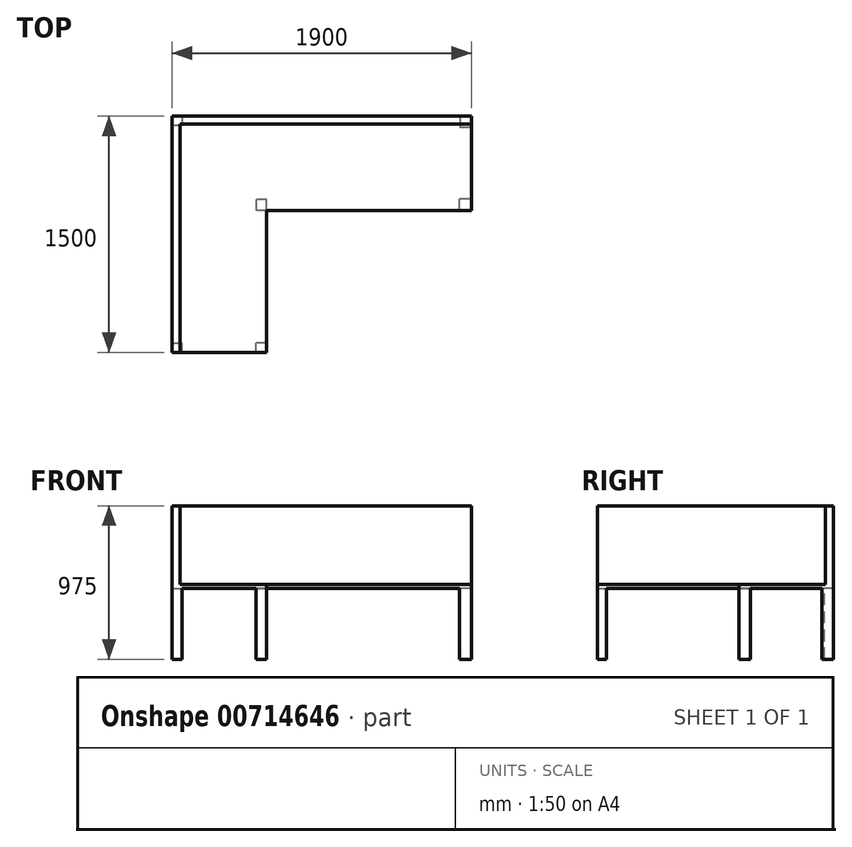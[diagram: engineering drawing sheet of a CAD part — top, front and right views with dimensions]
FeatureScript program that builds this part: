
annotation { "Feature Type Name" : "Feature", "Feature Type Description" : "" }
export const myFeature = defineFeature(function(context is Context, id is Id, definition is map)
    precondition{}
    {
        {
            var Q0;
            Q0=qCreatedBy(makeId("Top.planeOp"),FACE);
            var sketch = newSketch(context, id + "F0", { "sketchPlane" : qUnion([Q0])});
            skLineSegment(sketch, "E0.bottom", {"start": v(0, 0) * mm, "end": v(1900, 0) * mm});
            skLineSegment(sketch, "E0.top", {"start": v(600, -600) * mm, "end": v(1900, -600) * mm});
            skLineSegment(sketch, "E0.left", {"start": v(0, 0) * mm, "end": v(0, -600) * mm});
            skLineSegment(sketch, "E0.right", {"start": v(1900, 0) * mm, "end": v(1900, -600) * mm});
            skLineSegment(sketch, "E1.top", {"start": v(0, -1500) * mm, "end": v(600, -1500) * mm});
            skLineSegment(sketch, "E1.left", {"start": v(0, -600) * mm, "end": v(0, -1500) * mm});
            skLineSegment(sketch, "E1.right", {"start": v(600, -600) * mm, "end": v(600, -1500) * mm});
            skSolve(sketch);
        }
        {
            var Q0;
            Q0=makeQuery(id+"F0.imprint","IMPRINT",FACE,{"disambiguationData":[TD([[makeQuery(id+"F0.imprint","IMPRINT",EDGE,{"derivedFrom":sQuery(id+"F0.wireOp",EDGE,"E0.bottom")}),-1.0]])]});
            extrude(context, id + "F1", {"entities" : qUnion([Q0]), "depth" : 25 * mm, "offsetDistance" : 25 * mm});
        }
        {
            var Q0;
            Q0=makeQuery(id+"F1.opExtrude","CAP_FACE",FACE,{"disambiguationData":[OSD([sQuery(id+"F0.wireOp",EDGE,"E0.bottom"),sQuery(id+"F0.wireOp",EDGE,"E0.top"),sQuery(id+"F0.wireOp",EDGE,"E0.left"),sQuery(id+"F0.wireOp",EDGE,"E0.right"),sQuery(id+"F0.wireOp",EDGE,"vzaPsGMV-BrJu-azBP-gitS-3Vx8ohO2lJfg.top"),sQuery(id+"F0.wireOp",EDGE,"vzaPsGMV-BrJu-azBP-gitS-3Vx8ohO2lJfg.left"),sQuery(id+"F0.wireOp",EDGE,"vzaPsGMV-BrJu-azBP-gitS-3Vx8ohO2lJfg.right")])],"isStart":false});
            var sketch = newSketch(context, id + "F2", { "sketchPlane" : qUnion([Q0])});
            skLineSegment(sketch, "E2.bottom", {"start": v(1900, 0) * mm, "end": v(0, 0) * mm});
            skLineSegment(sketch, "E2.top", {"start": v(1900, -50) * mm, "end": v(50, -50) * mm});
            skLineSegment(sketch, "E2.left", {"start": v(1900, 0) * mm, "end": v(1900, -50) * mm});
            skLineSegment(sketch, "E2.right", {"start": v(0, 0) * mm, "end": v(0, -50) * mm});
            skLineSegment(sketch, "E3.bottom", {"start": v(0, -1500) * mm, "end": v(50, -1500) * mm});
            skLineSegment(sketch, "E3.left", {"start": v(0, -1500) * mm, "end": v(0, -231.52) * mm});
            skLineSegment(sketch, "E3.right", {"start": v(50, -1500) * mm, "end": v(50, -50) * mm});
            skSolve(sketch);
        }
        {
            var Q0;
            Q0=makeQuery(id+"F2.imprint","IMPRINT",FACE,{"disambiguationData":[TD([[makeQuery(id+"F2.imprint","IMPRINT",EDGE,{"derivedFrom":sQuery(id+"F2.wireOp",EDGE,"E2.bottom")}),-1.0]])]});
            extrude(context, id + "F3", {"entities" : qUnion([Q0]), "operationType" : NewBodyOperationType.ADD, "depth" : 500 * mm, "offsetDistance" : 25 * mm});
        }
        {
            var Q0;
            Q0=makeQuery(id+"F1.opExtrude","CAP_FACE",FACE,{"disambiguationData":[OSD([sQuery(id+"F0.wireOp",EDGE,"E0.bottom"),sQuery(id+"F0.wireOp",EDGE,"E0.top"),sQuery(id+"F0.wireOp",EDGE,"E0.left"),sQuery(id+"F0.wireOp",EDGE,"E0.right"),sQuery(id+"F0.wireOp",EDGE,"E1.top"),sQuery(id+"F0.wireOp",EDGE,"E1.left"),sQuery(id+"F0.wireOp",EDGE,"E1.right")])],"isStart":true});
            var sketch = newSketch(context, id + "F4", { "sketchPlane" : qUnion([Q0])});
            skLineSegment(sketch, "E4.bottom", {"start": v(0, 1500) * mm, "end": v(61.7, 1500) * mm});
            skLineSegment(sketch, "E4.top", {"start": v(0, 1442.18) * mm, "end": v(61.7, 1442.18) * mm});
            skLineSegment(sketch, "E4.left", {"start": v(0, 1500) * mm, "end": v(0, 1442.18) * mm});
            skLineSegment(sketch, "E4.right", {"start": v(61.7, 1500) * mm, "end": v(61.7, 1442.18) * mm});
            skLineSegment(sketch, "E5.bottom", {"start": v(600, 1500) * mm, "end": v(534.2, 1500) * mm});
            skLineSegment(sketch, "E5.top", {"start": v(600, 1442.18) * mm, "end": v(534.2, 1442.18) * mm});
            skLineSegment(sketch, "E5.left", {"start": v(600, 1500) * mm, "end": v(600, 1442.18) * mm});
            skLineSegment(sketch, "E5.right", {"start": v(534.2, 1500) * mm, "end": v(534.2, 1442.18) * mm});
            skLineSegment(sketch, "E6.bottom", {"start": v(0, 0) * mm, "end": v(61.7, 0) * mm});
            skLineSegment(sketch, "E6.top", {"start": v(0, 57.58) * mm, "end": v(61.7, 57.58) * mm});
            skLineSegment(sketch, "E6.left", {"start": v(0, 0) * mm, "end": v(0, 57.58) * mm});
            skLineSegment(sketch, "E6.right", {"start": v(61.7, 0) * mm, "end": v(61.7, 57.58) * mm});
            skLineSegment(sketch, "E7.bottom", {"start": v(1900, 0) * mm, "end": v(1829.1, 0) * mm});
            skLineSegment(sketch, "E7.top", {"start": v(1900, 72.53) * mm, "end": v(1829.1, 72.53) * mm});
            skLineSegment(sketch, "E7.left", {"start": v(1900, 0) * mm, "end": v(1900, 72.53) * mm});
            skLineSegment(sketch, "E7.right", {"start": v(1829.1, 0) * mm, "end": v(1829.1, 72.53) * mm});
            skLineSegment(sketch, "E8.bottom", {"start": v(1900, 600) * mm, "end": v(1826.1, 600) * mm});
            skLineSegment(sketch, "E8.top", {"start": v(1900, 527.09) * mm, "end": v(1826.1, 527.09) * mm});
            skLineSegment(sketch, "E8.left", {"start": v(1900, 600) * mm, "end": v(1900, 527.09) * mm});
            skLineSegment(sketch, "E8.right", {"start": v(1826.1, 600) * mm, "end": v(1826.1, 527.09) * mm});
            skLineSegment(sketch, "E9.bottom", {"start": v(600, 600) * mm, "end": v(537.2, 600) * mm});
            skLineSegment(sketch, "E9.top", {"start": v(600, 530.08) * mm, "end": v(537.2, 530.08) * mm});
            skLineSegment(sketch, "E9.left", {"start": v(600, 600) * mm, "end": v(600, 530.08) * mm});
            skLineSegment(sketch, "E9.right", {"start": v(537.2, 600) * mm, "end": v(537.2, 530.08) * mm});
            skSolve(sketch);
        }
        {
            var Q0;
            Q0=makeQuery(id+"F4.imprint","IMPRINT",FACE,{"disambiguationData":[TD([[makeQuery(id+"F4.imprint","IMPRINT",EDGE,{"derivedFrom":sQuery(id+"F4.wireOp",EDGE,"E4.bottom")}),-1.0]])]});
            var Q1;
            Q1=makeQuery(id+"F4.imprint","IMPRINT",FACE,{"disambiguationData":[TD([[makeQuery(id+"F4.imprint","IMPRINT",EDGE,{"derivedFrom":sQuery(id+"F4.wireOp",EDGE,"E5.bottom")}),-1.0]])]});
            var Q2;
            Q2=makeQuery(id+"F4.imprint","IMPRINT",FACE,{"disambiguationData":[TD([[makeQuery(id+"F4.imprint","IMPRINT",EDGE,{"derivedFrom":sQuery(id+"F4.wireOp",EDGE,"E9.bottom")}),1.0]])]});
            var Q3;
            Q3=makeQuery(id+"F4.imprint","IMPRINT",FACE,{"disambiguationData":[TD([[makeQuery(id+"F4.imprint","IMPRINT",EDGE,{"derivedFrom":sQuery(id+"F4.wireOp",EDGE,"E6.bottom")}),1.0]])]});
            var Q4;
            Q4=makeQuery(id+"F4.imprint","IMPRINT",FACE,{"disambiguationData":[TD([[makeQuery(id+"F4.imprint","IMPRINT",EDGE,{"derivedFrom":sQuery(id+"F4.wireOp",EDGE,"E8.bottom")}),-1.0]])]});
            var Q5;
            Q5=makeQuery(id+"F4.imprint","IMPRINT",FACE,{"disambiguationData":[TD([[makeQuery(id+"F4.imprint","IMPRINT",EDGE,{"derivedFrom":sQuery(id+"F4.wireOp",EDGE,"E7.bottom")}),1.0]])]});
            extrude(context, id + "F5", {"entities" : qUnion([Q0, Q1, Q2, Q3, Q4, Q5]), "operationType" : NewBodyOperationType.ADD, "depth" : 450 * mm, "offsetDistance" : 25 * mm});
        }
    });
